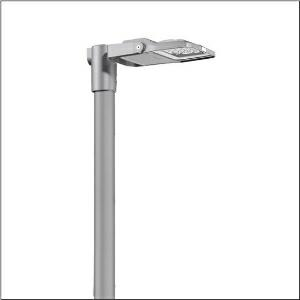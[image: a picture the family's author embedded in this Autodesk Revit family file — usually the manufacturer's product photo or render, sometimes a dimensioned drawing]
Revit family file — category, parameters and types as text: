
# Revit family: floodlight_fl_21_iq_micro___pl64_5xa7762a4e3a_dfd9
name_source: partatom
category: Lighting Fixtures
units: mm (PartAtom-declared; Revit-internal decimal feet)

## family parameters
Cut with Voids When Loaded = No
Host = Face
Light Source = No
Part Type = Normal
Room Calculation Point = No
Round Connector Dimension = Use Diameter
Shared = No

## types (1)
- --- (1 x LED, 2980 lm, 23.1 W, 4000K)
    Apparent Load = 23 VA
    CIE Flux Codes = 28 80 98 100 100
    Color Rendering = 70
    Color Temperature = 4000K
    Default Elevation = 1800 mm
    Description = Floodlight FL 21 iQ micro, floodlight, primary light control with lens, of PMMA, primary optical cover: protective disc, of toughened safety glass, transparent, light distribution: PL64, light emission: direct distribution, installation type: surface-mounted, lamps: LED, High Power LED, rated values: 2.980lm | 23,1W | 129lm/W (begin service life); end service life: 2.980lm | 23,8W; at 50% lumin. flux: 1.490lm | 11W | 135,5lm/W, colour temperature: 4000K, colour rendering: CRI > 70, light colour: 740, light setting 1 begin service life: 100% | 2.980lm | 23,1W | 129lm/W | 4.000K, light setting 1 end service life: 23,8W, further light settings possible, control: Auto-Match, Temp-Guard, Night-Set, Smart-Wire, Desk-Remote (wireless, voltage-free reading and setting of iQ features in the workshop via application-optimized NFC function/RFID function), optimised constant luminous flux control (CLO 2.0), Street-Remote, pre-setting: linear dimming characteristic, with terminal, 6-pole, mains connection: 220..240V, AC, 50/60Hz, luminaire housing, of diecast aluminium, powder-coated, SITECO metallic grey (DB 702S), corrosivity category C5 mid according to DIN EN ISO 12944suitable for swimming poolschlorine-resistant, sealing non-destructively replaceable, please order mast flange separately, mast bracket, of steel, galvanised, powder-coated, SITECO metallic grey (DB 702S), protection rating (complete): IP66, insulation class (complete): insulation class II (safety insulation), certification: CE, ENEC, VDE, protection symbol: D, impact resistance: IK07, permissible operating ambient temperature: -40..+40°C, permissible operating ambient temperature for outdoor applications: -40..+50°C, standard: DIN EN 12944, LABS conformity tested according to VDMA 24364:2018-05, packaging unit: 1 piece

Light Distribution: PL64
    Height = 65 mm
    Lamp = 1 x LED
    Lamp Light Flux = 2980 lm
    Lamp Power = 23.1 W
    Lamp count = 1
    Length = 312 mm
    Luminous efficacy = 129 lm/W
    Manufacturer = Siteco
    ModVariant = No
    Model = 5XA7762A4E3A
    Number of Poles = 1
    OnlyDefault = Yes
    Power Factor = 1
    Product Name = Floodlight FL 21 iQ micro | PL64
    Product group = floodlight | pylon annexe
    ProductGroupID = 6201
    Protection Class = Protection class II
    Protection Degree = IP 66
    RLX_Detail_Level = 1
    RLX_Emergency_Light_Flux = 0 lm
    RLX_Emergency_Type = 0
    RLX_Emergency_Type_DB = No
    RlxData = <blob elided: 101997 chars, md5=ec868556>
    Socket = socket
    Standby Power = 0 W
    System Light Flux = 2980 lm
    System Power = 23 W
    Type Comments = factory setting: luminous flux: 100 % | dim-lin: 254 | 455 mA
    Type Image = l_1007121.jpg
    URL = http://relux.com
    VarID = @adj_179237
    Voltage = 0 V
    Weight = 0.00 kg
    Width = 230 mm

## geometry (parser evidence)
native form markers: Blend x4, Sweep x11
no freeform markers — native parametric forms only
